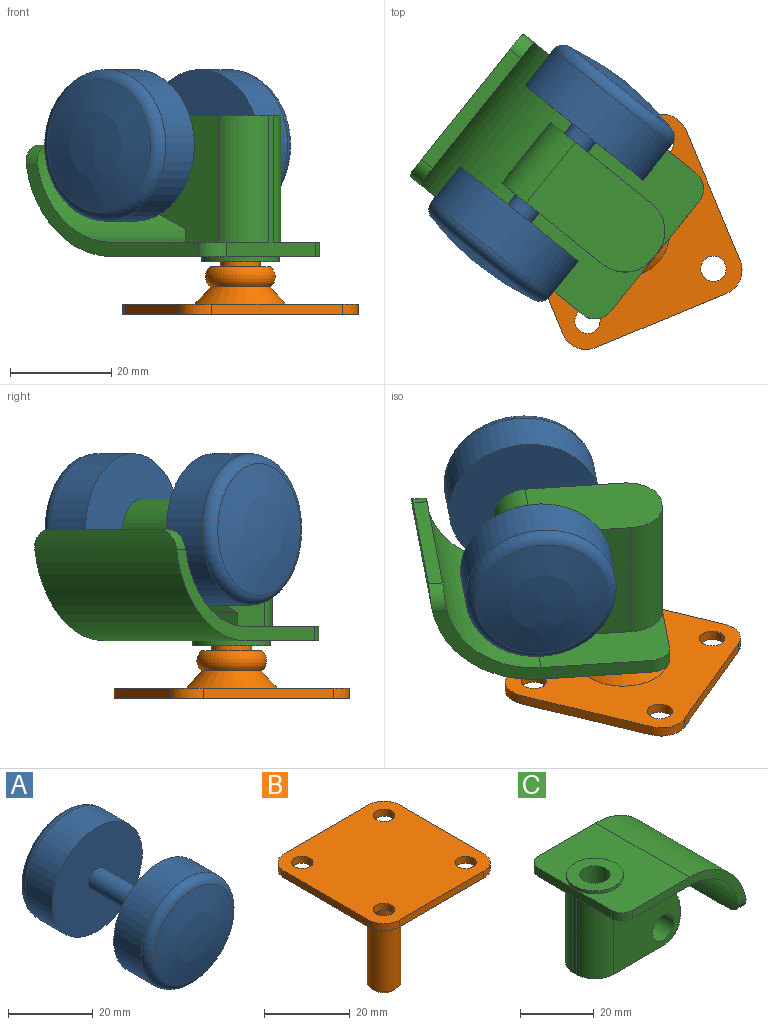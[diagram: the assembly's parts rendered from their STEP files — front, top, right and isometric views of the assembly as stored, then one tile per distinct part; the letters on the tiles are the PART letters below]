
ASSEMBLY  parts=3 mates=2
PART A: 9 faces, bbox 32.5x46.5x32.5 mm
  f0: sphere r=57.25mm, area 543.9mm2, adj f8
  f1: sphere r=57.25mm, area 543.9mm2, adj f2
  f2: torus R=12.5mm, axis (0,-1,0), area 301.4mm2, adj f1,f3
  f3: cylinder r=15mm len=30mm, axis (0,-1,0), area 853.3mm2, adj f2,f4
  f4: plane 30x30mm, normal (0,-1,0), area 678.6mm2, adj f3,f5
  f5: cylinder r=3mm len=20.5mm, axis (0,-1,0), area 386.4mm2, adj f4,f6
  f6: plane 30x30mm, normal (0,1,0), area 678.6mm2, adj f5,f7
  f7: cylinder r=15mm len=30mm, axis (0,-1,0), area 853.3mm2, adj f6,f8
  f8: torus R=12.5mm, axis (0,-1,0), area 301.4mm2, adj f0,f7
PART B: 20 faces, bbox 38x38x35.4 mm
  f0: cone r=5.9mm half-angle=42.4deg, axis (0,0,1), area 215.4mm2, adj f1,f19
  f1: torus R=4.4mm, axis (0,0,1), area 191mm2, adj f0,f2
  f2: plane 11.8x11.8mm, normal (0,0,-1), area 60.3mm2, adj f1,f3
  f3: cylinder r=3.95mm len=24.8mm, axis (0,0,1), area 615.5mm2, adj f2,f4
  f4: cone r=2.75mm half-angle=45deg, axis (0,0,1), area 35.7mm2, adj f3,f5
  f5: plane 5.5x5.5mm, normal (0,0,-1), area 23.8mm2, adj f4
  f6: cylinder r=5mm len=5mm, axis (0,0,-1), area 15.7mm2, adj f7,f17,f18,f19
  f7: plane 28x2mm, normal (0,-1,0), area 56mm2, adj f6,f8,f18,f19
  f8: cylinder r=5mm len=5mm, axis (0,0,-1), area 15.7mm2, adj f7,f9,f18,f19
  f9: plane 28x2mm, normal (1,0,0), area 56mm2, adj f8,f10,f18,f19
  f10: cylinder r=5mm len=5mm, axis (0,0,-1), area 15.7mm2, adj f9,f11,f18,f19
  f11: plane 28x2mm, normal (0,1,0), area 56mm2, adj f10,f12,f18,f19
  f12: cylinder r=5mm len=5mm, axis (0,0,-1), area 15.7mm2, adj f11,f17,f18,f19
  f13: cylinder r=2.5mm len=5mm, axis (0,0,-1), area 31.4mm2, adj f18,f19
  f14: cylinder r=2.5mm len=5mm, axis (0,0,-1), area 31.4mm2, adj f18,f19
  f15: cylinder r=2.5mm len=5mm, axis (0,0,-1), area 31.4mm2, adj f18,f19
  f16: cylinder r=2.5mm len=5mm, axis (0,0,-1), area 31.4mm2, adj f18,f19
  f17: plane 28x2mm, normal (-1,0,0), area 56mm2, adj f6,f12,f18,f19
  f18: plane 38x38mm, normal (0,0,1), area 1344mm2, adj f6,f7,f8,f9,f10,f11,f12,f13
  f19: plane 38x38mm, normal (0,0,-1), area 1089.5mm2, adj f0,f6,f7,f8,f9,f10,f11,f12
PART C: 27 faces, bbox 48x36x29 mm
  f0: cylinder r=6.3mm len=15.4mm, axis (0,1,0), area 152.4mm2, adj f1,f7,f8,f9
  f1: plane 15.4x3.16mm, normal (1,0,0), area 48.6mm2, adj f0,f2,f8,f9
  f2: cylinder r=8.8mm len=15.4mm, axis (0,1,0), area 159.3mm2, adj f1,f3,f8,f9
  f3: plane 15.4x11.79mm, normal (0.39,0,0.92), area 196.8mm2, adj f2,f4,f8,f9
  f4: plane 15.4x2.7mm, normal (1,0,0), area 41.6mm2, adj f3,f8,f9,f10
  f5: plane 28x28mm, normal (-1,0,0), area 113.7mm2, adj f7,f10,f14,f17,f18,f20,f22
  f6: cylinder r=4.1mm len=15.4mm, axis (0,1,0), area 396.7mm2, adj f8,f9
  f7: plane 26.4x15.4mm, normal (0,0,-1), area 385.5mm2, adj f0,f5,f8,f9,f17,f18
  f8: plane 25.7x25.2mm, normal (0,-1,0), area 472mm2, adj f0,f1,f2,f3,f4,f6,f7,f10
  f9: plane 25.7x25.2mm, normal (0,1,0), area 472mm2, adj f0,f1,f2,f3,f4,f6,f7,f10
  f10: plane 36x26mm, normal (0,0,-1), area 711.5mm2, adj f4,f5,f8,f9,f11,f15,f16,f17
  f11: cylinder r=19.2mm len=36mm, axis (0,1,0), area 1078.9mm2, adj f10,f12,f15,f16,f19,f21
  f12: plane 28x2.8mm, normal (0,0,-1), area 78.4mm2, adj f11,f13,f19,f21
  f13: cylinder r=22mm len=36mm, axis (0,1,0), area 1237.2mm2, adj f12,f14,f15,f16,f19,f21
  f14: plane 36x26mm, normal (0,0,1), area 742.9mm2, adj f5,f13,f15,f16,f20,f22,f23
  f15: plane 43.63x18mm, normal (0,-1,0), area 140.9mm2, adj f10,f11,f13,f14,f21,f22
  f16: plane 43.63x18mm, normal (0,1,0), area 140.9mm2, adj f10,f11,f13,f14,f19,f20
  f17: cylinder r=7mm len=25.2mm, axis (0,0,-1), area 277.1mm2, adj f5,f7,f9,f10
  f18: cylinder r=7mm len=25.2mm, axis (0,0,1), area 277.1mm2, adj f5,f7,f8,f10
  f19: cylinder r=4mm len=4mm, axis (1,0,0), area 17.7mm2, adj f11,f12,f13,f16
  f20: cylinder r=4mm len=4mm, axis (0,0,-1), area 17.6mm2, adj f5,f10,f14,f16
  f21: cylinder r=4mm len=4mm, axis (-1,0,0), area 17.7mm2, adj f11,f12,f13,f15
  f22: cylinder r=4mm len=4mm, axis (0,0,1), area 17.6mm2, adj f5,f10,f14,f15
  f23: cylinder r=7.7mm len=15.4mm, axis (0,0,1), area 48.4mm2, adj f14,f24
  f24: plane 15.4x15.4mm, normal (0,0,1), area 133.5mm2, adj f23,f25
  f25: cylinder r=4.1mm len=25mm, axis (0,0,1), area 644mm2, adj f24,f26
  f26: plane 8.2x8.2mm, normal (0,0,1), area 52.8mm2, adj f25
PLACE A rot(axis=(0,0,-1),38.7deg) t=(-33.4,-3.87,15.25)mm
PLACE B rot(axis=(0.2,-0.98,0),180deg) t=(-36.05,-22.48,15.25)mm fixed
PLACE C rot(axis=(-0.33,-0.94,0),180deg) t=(-33.4,-3.87,15.25)mm
MATE revolute C.f23 <-> B.f0  axis (0,0,-1) through (-19.01,-15.42,17.25)mm
MATE revolute A.f3 <-> C.f6  axis (-0.63,-0.78,0) through (-33.4,-3.87,15.25)mm
